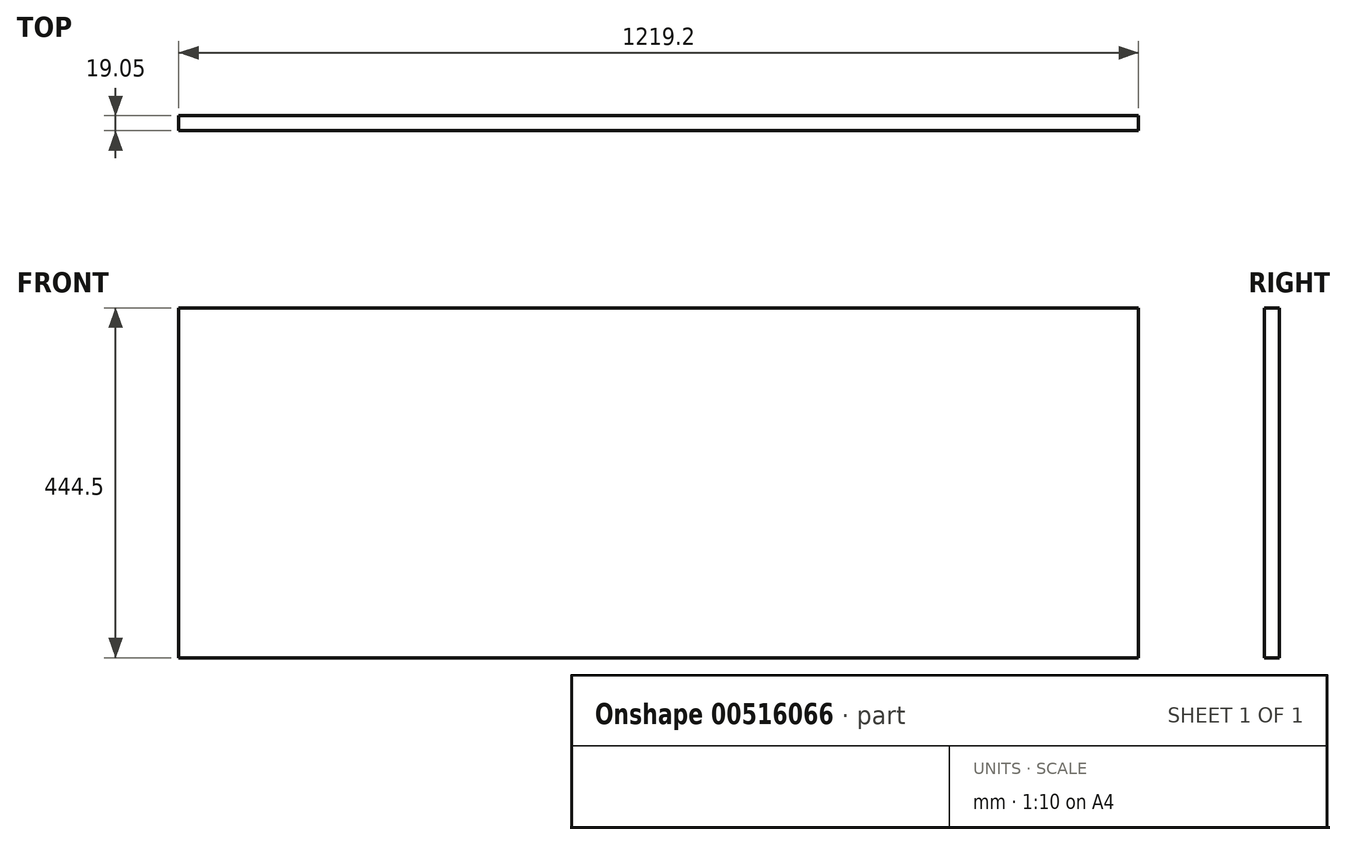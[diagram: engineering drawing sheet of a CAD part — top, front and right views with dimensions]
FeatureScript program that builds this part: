
annotation { "Feature Type Name" : "Feature", "Feature Type Description" : "" }
export const myFeature = defineFeature(function(context is Context, id is Id, definition is map)
    precondition{}
    {
        {
            var Q0;
            Q0=qCreatedBy(makeId("Front.planeOp"),FACE);
            var sketch = newSketch(context, id + "F0", { "sketchPlane" : qUnion([Q0])});
            skLineSegment(sketch, "E0.bottom", {"start": v(609.6, -222.25) * mm, "end": v(-609.6, -222.25) * mm});
            skLineSegment(sketch, "E0.top", {"start": v(609.6, 222.25) * mm, "end": v(-609.6, 222.25) * mm});
            skLineSegment(sketch, "E0.left", {"start": v(609.6, -222.25) * mm, "end": v(609.6, 222.25) * mm});
            skLineSegment(sketch, "E0.right", {"start": v(-609.6, -222.25) * mm, "end": v(-609.6, 222.25) * mm});
            skPoint(sketch, "E0.middle", {"position": v(0, 0) * mm});
            skSolve(sketch);
        }
        {
            var Q0;
            Q0=makeQuery(id+"F0.imprint","IMPRINT",FACE,{"disambiguationData":[TD([[makeQuery(id+"F0.imprint","IMPRINT",EDGE,{"derivedFrom":sQuery(id+"F0.wireOp",EDGE,"E0.bottom")}),-1.0]])]});
            extrude(context, id + "F1", {"entities" : qUnion([Q0]), "depth" : 19.05 * mm, "offsetDistance" : 25.4 * mm});
        }
    });
